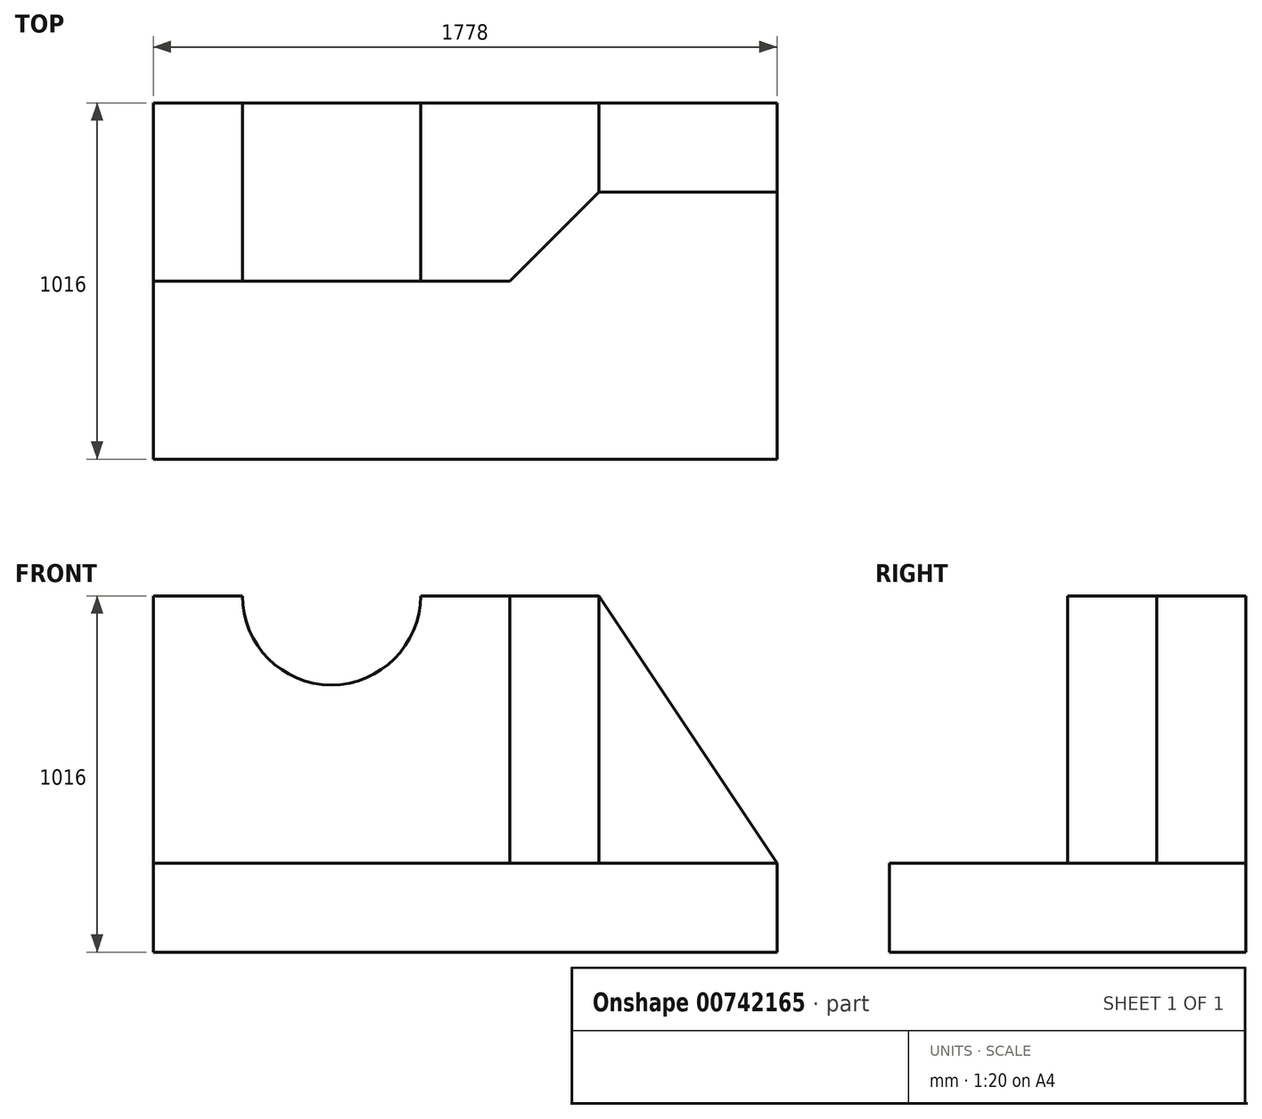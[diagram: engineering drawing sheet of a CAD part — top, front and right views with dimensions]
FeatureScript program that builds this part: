
annotation { "Feature Type Name" : "Feature", "Feature Type Description" : "" }
export const myFeature = defineFeature(function(context is Context, id is Id, definition is map)
    precondition{}
    {
        {
            var Q0;
            Q0=qCreatedBy(makeId("Front.planeOp"),FACE);
            var sketch = newSketch(context, id + "F0", { "sketchPlane" : qUnion([Q0])});
            skLineSegment(sketch, "E0", {"start": v(0, 0) * mm, "end": v(0, 1016) * mm});
            skLineSegment(sketch, "E1", {"start": v(0, 0) * mm, "end": v(1778, 0) * mm});
            skLineSegment(sketch, "E2", {"start": v(1778, 0) * mm, "end": v(1778, 254) * mm});
            skLineSegment(sketch, "E3", {"start": v(0, 1016) * mm, "end": v(1016, 1016) * mm});
            skLineSegment(sketch, "E4", {"start": v(1778, 254) * mm, "end": v(0, 254) * mm});
            skLineSegment(sketch, "E5", {"start": v(0, 1016) * mm, "end": v(508, 1016) * mm});
            skLineSegment(sketch, "E6", {"start": v(508, 1016) * mm, "end": v(1016, 1016) * mm});
            skCircle(sketch, "E7", {"center": v(508, 1016) * mm, "radius": 254 * mm});
            skLineSegment(sketch, "E8", {"start": v(1016, 1016) * mm, "end": v(1016, 254) * mm});
            skLineSegment(sketch, "E9", {"start": v(1016, 1016) * mm, "end": v(1270, 1016) * mm});
            skLineSegment(sketch, "E10", {"start": v(1270, 1016) * mm, "end": v(1270, 254) * mm});
            skLineSegment(sketch, "E11", {"start": v(1270, 1016) * mm, "end": v(1778, 254) * mm});
            skSolve(sketch);
        }
        {
            var Q0;
            {var subQ3=sQuery(id+"F0.wireOp",EDGE,"E10");var subQ6=makeQuery(id+"F0.imprint","IMPRINT",EDGE,{"derivedFrom":subQ3});var subQ7=sQuery(id+"F0.wireOp",EDGE,"E8");var subQ10=makeQuery(id+"F0.imprint","IMPRINT",EDGE,{"derivedFrom":subQ7});var subQ13=sQuery(id+"F0.wireOp",EDGE,"E3");var subQ15=makeQuery(id+"F0.imprint","IMPRINT",VERTEX,{"derivedFrom":subQ13});var subQ16=makeQuery(id+"F0.imprint","IMPRINT",EDGE,{"disambiguationData":[TD([[subQ15,-1.0]])],"derivedFrom":subQ13});var subQ23=sQuery(id+"F0.wireOp",EDGE,"E1");Q0=qUnion([makeQuery(id+"F0.imprint","IMPRINT",FACE,{"disambiguationData":[TD([[subQ10,-1.0]])]}),makeQuery(id+"F0.imprint","IMPRINT",FACE,{"disambiguationData":[TD([[subQ16,1.0]])]}),makeQuery(id+"F0.imprint","IMPRINT",FACE,{"disambiguationData":[TD([[makeQuery(id+"F0.imprint","IMPRINT",EDGE,{"derivedFrom":subQ23}),1.0]])]}),makeQuery(id+"F0.imprint","IMPRINT",FACE,{"disambiguationData":[TD([[subQ16,-1.0]])]}),makeQuery(id+"F0.imprint","IMPRINT",FACE,{"disambiguationData":[TD([[subQ10,1.0]])]}),makeQuery(id+"F0.imprint","IMPRINT",FACE,{"disambiguationData":[TD([[subQ6,1.0]])]})]);}
            extrude(context, id + "F1", {"entities" : qUnion([Q0]), "depth" : 1016 * mm, "offsetDistance" : 25.4 * mm});
        }
        {
            var Q0;
            Q0=makeQuery(id+"F1.opExtrude","CAP_FACE",FACE,{"disambiguationData":[OSD([sQuery(id+"F0.wireOp",EDGE,"E0"),sQuery(id+"F0.wireOp",EDGE,"E1"),sQuery(id+"F0.wireOp",EDGE,"E2"),sQuery(id+"F0.wireOp",EDGE,"E3"),sQuery(id+"F0.wireOp",EDGE,"E7"),sQuery(id+"F0.wireOp",EDGE,"E9"),sQuery(id+"F0.wireOp",EDGE,"E11")])],"isStart":false});
            var sketch = newSketch(context, id + "F2", { "sketchPlane" : qUnion([Q0])});
            skCircle(sketch, "E12", {"center": v(508, 1016) * mm, "radius": 254 * mm});
            skSolve(sketch);
        }
        {
            var Q0;
            Q0 = qSketchRegion(id + "F2", true);
            extrude(context, id + "F3", {"entities" : qUnion([Q0]), "operationType" : NewBodyOperationType.REMOVE, "oppositeDirection" : true, "depth" : 1064.26 * mm, "offsetDistance" : 25.4 * mm});
        }
        {
            var Q0;
            Q0=makeQuery(id+"F1.opExtrude","CAP_FACE",FACE,{"disambiguationData":[OSD([sQuery(id+"F0.wireOp",EDGE,"E0"),sQuery(id+"F0.wireOp",EDGE,"E1"),sQuery(id+"F0.wireOp",EDGE,"E2"),sQuery(id+"F0.wireOp",EDGE,"E3"),sQuery(id+"F0.wireOp",EDGE,"E7"),sQuery(id+"F0.wireOp",EDGE,"E9"),sQuery(id+"F0.wireOp",EDGE,"E11")])],"isStart":false});
            var sketch = newSketch(context, id + "F4", { "sketchPlane" : qUnion([Q0])});
            skLineSegment(sketch, "E13", {"start": v(1270, 1016) * mm, "end": v(1270, 254) * mm});
            skLineSegment(sketch, "E14", {"start": v(1270, 254) * mm, "end": v(1778, 254) * mm});
            skLineSegment(sketch, "E15", {"start": v(0, 1016) * mm, "end": v(0, 254) * mm});
            skLineSegment(sketch, "E16", {"start": v(0, 254) * mm, "end": v(1270, 254) * mm});
            skLineSegment(sketch, "E17", {"start": v(0, 1016) * mm, "end": v(254, 1016) * mm});
            skLineSegment(sketch, "E18", {"start": v(254, 1016) * mm, "end": v(1270, 1016) * mm});
            skLineSegment(sketch, "E19", {"start": v(1270, 254) * mm, "end": v(1270, 1016) * mm});
            skSolve(sketch);
        }
        {
            var Q0;
            Q0 = qSketchRegion(id + "F4", true);
            var Q1;
            Q1=makeQuery(id+"F4.imprint","IMPRINT",FACE,{"disambiguationData":[TD([[makeQuery(id+"F4.imprint","IMPRINT",EDGE,{"derivedFrom":sQuery(id+"F4.wireOp",EDGE,"E14")}),1.0]])]});
            extrude(context, id + "F5", {"entities" : qUnion([Q0, Q1]), "operationType" : NewBodyOperationType.REMOVE, "oppositeDirection" : true, "depth" : 508 * mm, "offsetDistance" : 25.4 * mm});
        }
        {
            var Q0;
            Q0=makeQuery(id+"F5.boolean.opBoolean","COPY",FACE,{"derivedFrom":makeQuery(id+"F5.opExtrude","CAP_FACE",FACE,{"disambiguationData":[OSD([sQuery(id+"F0.wireOp",EDGE,"E11"),sQuery(id+"F4.wireOp",EDGE,"E14"),sQuery(id+"F4.wireOp",EDGE,"E15"),sQuery(id+"F4.wireOp",EDGE,"E16"),sQuery(id+"F4.wireOp",EDGE,"E17"),sQuery(id+"F4.wireOp",EDGE,"E18")])],"isStart":false})});
            var sketch = newSketch(context, id + "F6", { "sketchPlane" : qUnion([Q0])});
            skLineSegment(sketch, "E20", {"start": v(1270, 1016) * mm, "end": v(1270, 254) * mm});
            skLineSegment(sketch, "E21", {"start": v(1270, 254) * mm, "end": v(1778, 254) * mm});
            skLineSegment(sketch, "E22", {"start": v(1778, 254) * mm, "end": v(1270, 1016) * mm});
            skSolve(sketch);
        }
        {
            var Q0;
            Q0 = qSketchRegion(id + "F6", true);
            extrude(context, id + "F7", {"entities" : qUnion([Q0]), "operationType" : NewBodyOperationType.REMOVE, "oppositeDirection" : true, "depth" : 254 * mm, "offsetDistance" : 25.4 * mm});
        }
        {
            var Q0;
            Q0=makeQuery(id+"F1.opExtrude","SWEPT_FACE",FACE,{"disambiguationData":[OSD([sQuery(id+"F0.wireOp",EDGE,"E3"),sQuery(id+"F0.wireOp",EDGE,"E9")])]});
            var sketch = newSketch(context, id + "F8", { "sketchPlane" : qUnion([Q0])});
            skLineSegment(sketch, "E23", {"start": v(1270, -254) * mm, "end": v(1016, -508) * mm});
            skLineSegment(sketch, "E24", {"start": v(1270, -254) * mm, "end": v(1270, -508) * mm});
            skLineSegment(sketch, "E25", {"start": v(1270, -508) * mm, "end": v(1016, -508) * mm});
            skSolve(sketch);
        }
        {
            var Q0;
            Q0 = qSketchRegion(id + "F8", true);
            extrude(context, id + "F9", {"entities" : qUnion([Q0]), "operationType" : NewBodyOperationType.REMOVE, "oppositeDirection" : true, "depth" : 762 * mm, "offsetDistance" : 25.4 * mm});
        }
    });
